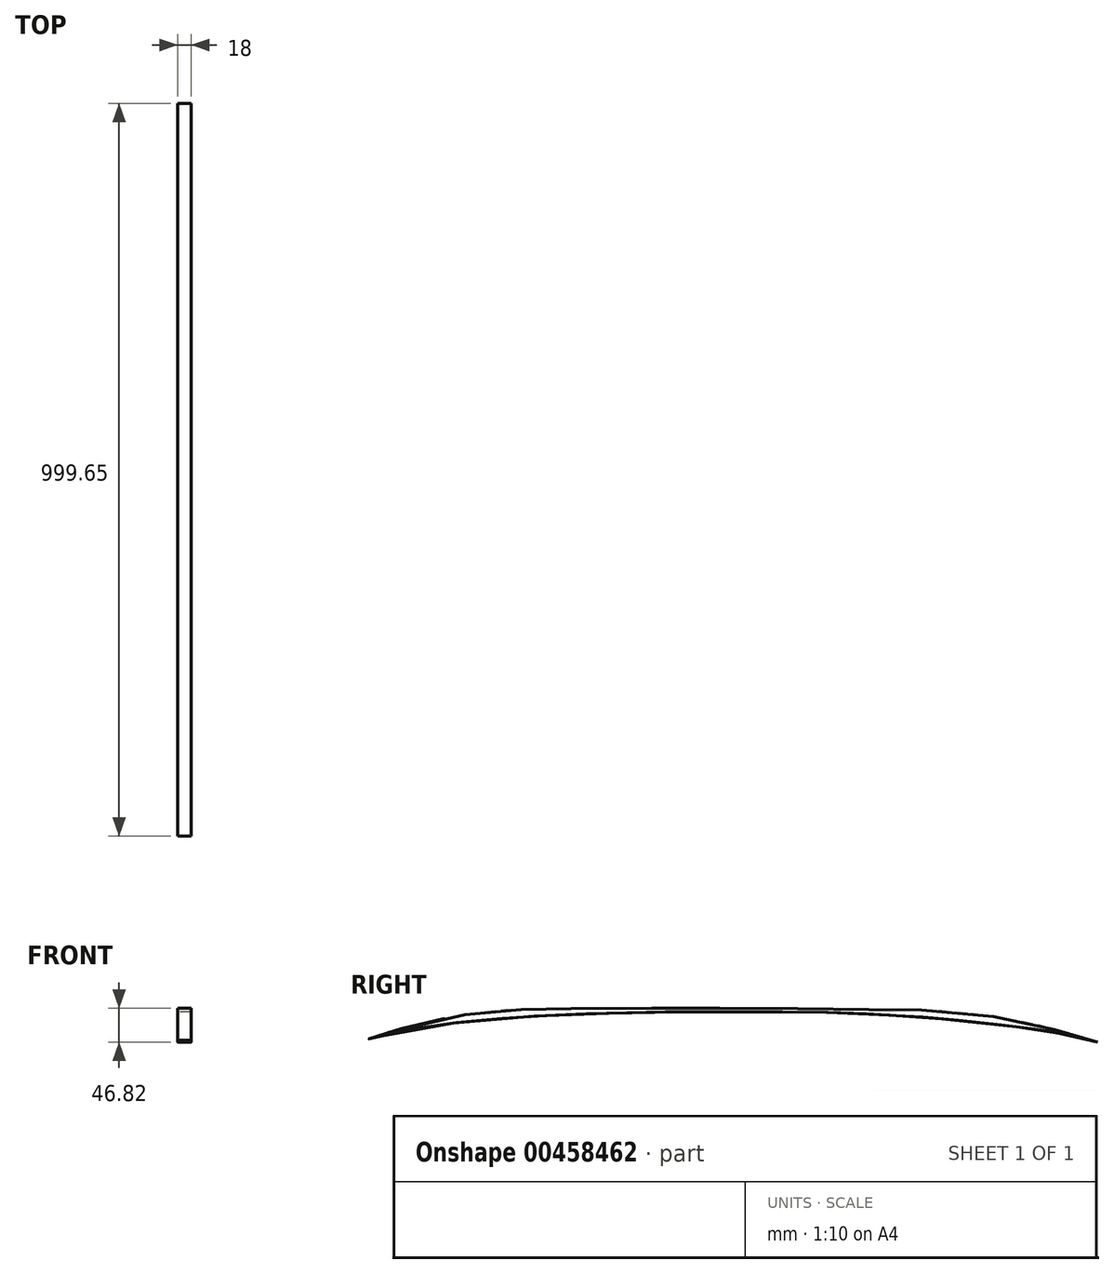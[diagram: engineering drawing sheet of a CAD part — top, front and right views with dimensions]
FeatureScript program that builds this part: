
annotation { "Feature Type Name" : "Feature", "Feature Type Description" : "" }
export const myFeature = defineFeature(function(context is Context, id is Id, definition is map)
    precondition{}
    {
        {
            var Q0;
            Q0=qCreatedBy(makeId("Right.planeOp"),FACE);
            var sketch = newSketch(context, id + "F0", { "sketchPlane" : qUnion([Q0])});
            skFitSpline(sketch, "E0", {"points": [v(497.12, 46) * mm, v(461.99, 56.6) * mm, v(405.12, 72.04) * mm, v(287.97, 88.59) * mm, v(215.92, 90.6) * mm, v(147.84, 91.6) * mm, v(7.52, 92.74) * mm, v(-85.35, 92.7) * mm, v(-223.46, 91.93) * mm, v(-279.3, 91.06) * mm, v(-327.06, 88.61) * mm, v(-443.34, 67.4) * mm, v(-502.53, 48.84) * mm, v(-458.73, 60.3) * mm, v(-318, 78.55) * mm, v(-193.6, 85.16) * mm, v(-85.25, 87.46) * mm, v(7.6, 87.4) * mm, v(147.84, 86.21) * mm, v(222.15, 82.66) * mm, v(280, 78.63) * mm, v(394.15, 66.3) * mm, v(435, 60.24) * mm, v(466.64, 53.59) * mm, v(497.12, 46) * mm]});
            skSolve(sketch);
        }
        {
            var Q0;
            Q0=makeQuery(id+"F0.imprint","IMPRINT",FACE,{"disambiguationData":[TD([[makeQuery(id+"F0.imprint","IMPRINT",EDGE,{"derivedFrom":sQuery(id+"F0.wireOp",EDGE,"E0")}),1.0]])]});
            extrude(context, id + "F1", {"entities" : qUnion([Q0]), "depth" : 18 * mm});
        }
    });
